# Revit family: Haworth_XSeries_Locker_Cubby6Doors
name_source: partatom
category: Furniture Systems
units: mm (PartAtom-declared; Revit-internal decimal feet)

## family parameters
Always vertical = Yes
Cut with Voids When Loaded = No
OmniClass Number = 23.40.70.14.64.21
OmniClass Title = Systems Furniture
Part Type = Normal
Room Calculation Point = No
Round Connector Dimension = Use Diameter
Shared = No
Work Plane-Based = No

## types (3) — shared parameters
Actual Depth = 18 3/4"
Actual Width = 36"
Assembly Code = E2020200
Base Height = 1 7/8"
Classic Pull = No
Crescent Pull = No
Custom Depth = No
Custom Height = No
Custom Size = No
Custom Width = No
Depth = 18 3/4"
Description = Haworth XSeries Locker - Cubby 6 Doors
Door 1 = Yes
Door 3 = Yes
Door 7 = Yes
Door 9 = Yes
Door Gap = 1/8"
Door Offset = 1/16"
J Pull = No
Linear Pull = Yes
Manufacturer = Haworth
Max. Depth = 18 3/4"
Max. Height = 63 1/2"
Max. Width = 36"
Min. Depth = 18 3/4"
Min. Height = 39 1/2"
Min. Width = 36"
Model = JA18
Panel Thickness = 3/4"
Panel Thickness Half = 3/8"
Pull Ellipse = No
Pull Finish = Haworth _ Metal _ Brushed Aluminum
Radius Pull = No
Revision Number = 3
Size = Verify Final Dim. w/ Haworth
Standard Depths = 18.75 in.
Standard Heights = 39.5, 51.5, 63.5 in.
Standard Widths = 36 in.
Sustainability Info = https://www.haworth.com
Taper Pull = No
Top Height = 1 1/4"
URL = http://www.haworth.com
URL - Product = https://www.haworth.com
Warranty = https://cdn.shopify.com
Width = 36"

## per-type parameters (varying)
| type | Actual Height | Door 2 | Door 4 | Door 6 | Door 8 | Door Height | Door Width | Doors 2H 3W | Doors 3H 2W | Height | Pull Height | Pull Offset Centerline |
| 18d 36w 63h | 63 1/2" | No | Yes | Yes | No | 20" | 17 7/8" | No | Yes | 63 1/2" | 10" | 16 3/8" |
| 18d 36w 51h | 51 1/2" | Yes | No | No | Yes | 24 1/16" | 11 13/16" | Yes | No | 51 1/2" | 12 1/32" | 10 5/16" |
| 18d 36w 39h | 39 1/2" | Yes | No | No | Yes | 18 1/16" | 11 13/16" | Yes | No | 39 1/2" | 9 1/32" | 10 5/16" |

## geometry (parser evidence)
native form markers: Sweep x5
no freeform markers — native parametric forms only
